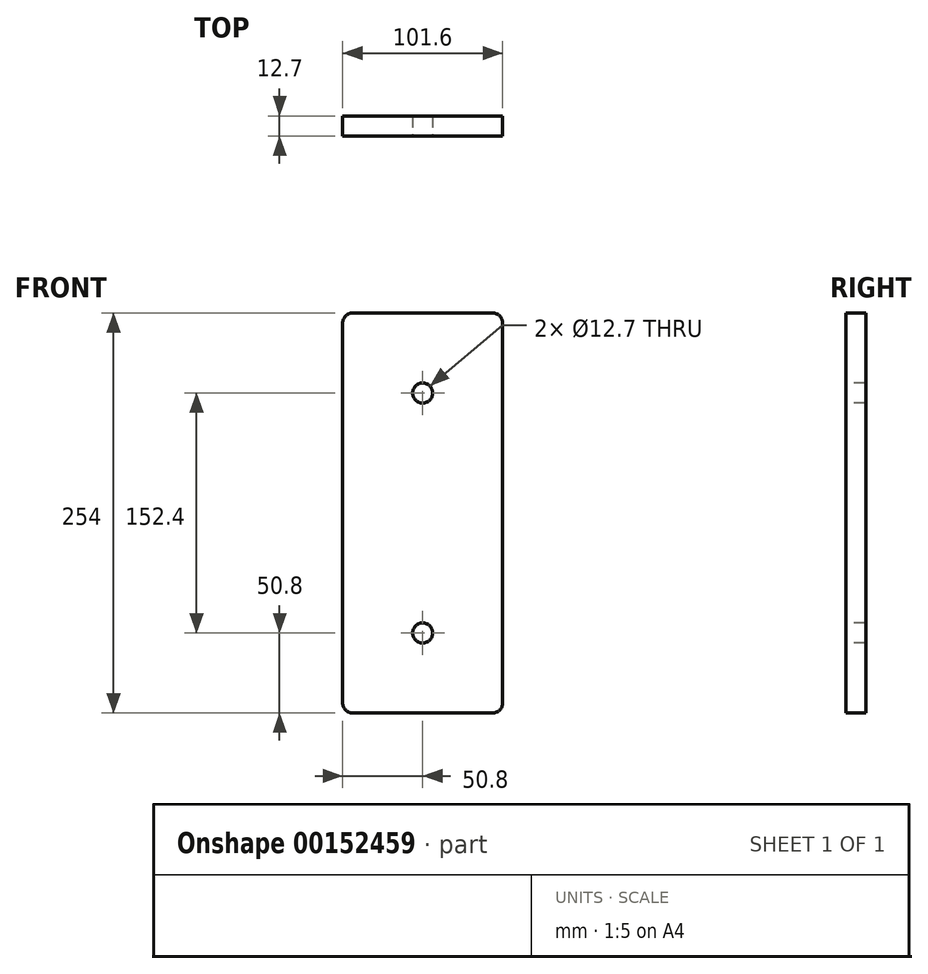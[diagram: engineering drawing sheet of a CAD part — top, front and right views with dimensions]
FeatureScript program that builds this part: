
annotation { "Feature Type Name" : "Feature", "Feature Type Description" : "" }
export const myFeature = defineFeature(function(context is Context, id is Id, definition is map)
    precondition{}
    {
        {
            var Q0;
            Q0=qCreatedBy(makeId("Front.planeOp"),FACE);
            var sketch = newSketch(context, id + "F0", { "sketchPlane" : qUnion([Q0])});
            skLineSegment(sketch, "E0.bottom", {"start": v(0, 0) * mm, "end": v(101.6, 0) * mm});
            skLineSegment(sketch, "E0.top", {"start": v(0, -254) * mm, "end": v(101.6, -254) * mm});
            skLineSegment(sketch, "E0.left", {"start": v(0, 0) * mm, "end": v(0, -254) * mm});
            skLineSegment(sketch, "E0.right", {"start": v(101.6, 0) * mm, "end": v(101.6, -254) * mm});
            skSolve(sketch);
        }
        {
            var Q0;
            Q0 = qSketchRegion(id + "F0", true);
            extrude(context, id + "F1", {"entities" : qUnion([Q0]), "depth" : 12.7 * mm});
        }
        {
            var Q0;
            Q0=makeQuery(id+"F1.opExtrude","SWEPT_EDGE",EDGE,{"disambiguationData":[OSD([sQuery(id+"F0.wireOp",EDGE,"E0.bottom"),sQuery(id+"F0.wireOp",EDGE,"E0.right")])]});
            var Q1;
            Q1=makeQuery(id+"F1.opExtrude","SWEPT_EDGE",EDGE,{"disambiguationData":[OSD([sQuery(id+"F0.wireOp",EDGE,"E0.bottom"),sQuery(id+"F0.wireOp",EDGE,"E0.left")])]});
            var Q2;
            Q2=makeQuery(id+"F1.opExtrude","SWEPT_EDGE",EDGE,{"disambiguationData":[OSD([sQuery(id+"F0.wireOp",EDGE,"E0.top"),sQuery(id+"F0.wireOp",EDGE,"E0.right")])]});
            var Q3;
            Q3=makeQuery(id+"F1.opExtrude","SWEPT_EDGE",EDGE,{"disambiguationData":[OSD([sQuery(id+"F0.wireOp",EDGE,"E0.top"),sQuery(id+"F0.wireOp",EDGE,"E0.left")])]});
            fillet(context, id + "F2", {"entities" : qUnion([Q0, Q1, Q2, Q3]), "radius" : 6.35 * mm, "tangentPropagation" : true, "allowEdgeOverflow" : false});
        }
        {
            var Q0;
            Q0=makeQuery(id+"F1.opExtrude","CAP_FACE",FACE,{"disambiguationData":[OSD([sQuery(id+"F0.wireOp",EDGE,"E0.bottom"),sQuery(id+"F0.wireOp",EDGE,"E0.top"),sQuery(id+"F0.wireOp",EDGE,"E0.left"),sQuery(id+"F0.wireOp",EDGE,"E0.right")])],"isStart":false});
            var sketch = newSketch(context, id + "F3", { "sketchPlane" : qUnion([Q0])});
            skCircle(sketch, "E1", {"center": v(50.8, -50.8) * mm, "radius": 6.35 * mm});
            skCircle(sketch, "E2", {"center": v(50.8, -203.2) * mm, "radius": 6.35 * mm});
            skSolve(sketch);
        }
        {
            var Q0;
            Q0 = qSketchRegion(id + "F3", true);
            extrude(context, id + "F4", {"entities" : qUnion([Q0]), "operationType" : NewBodyOperationType.REMOVE, "endBound" : BoundingType.THROUGH_ALL, "oppositeDirection" : true, "depth" : 25.4 * mm});
        }
    });
